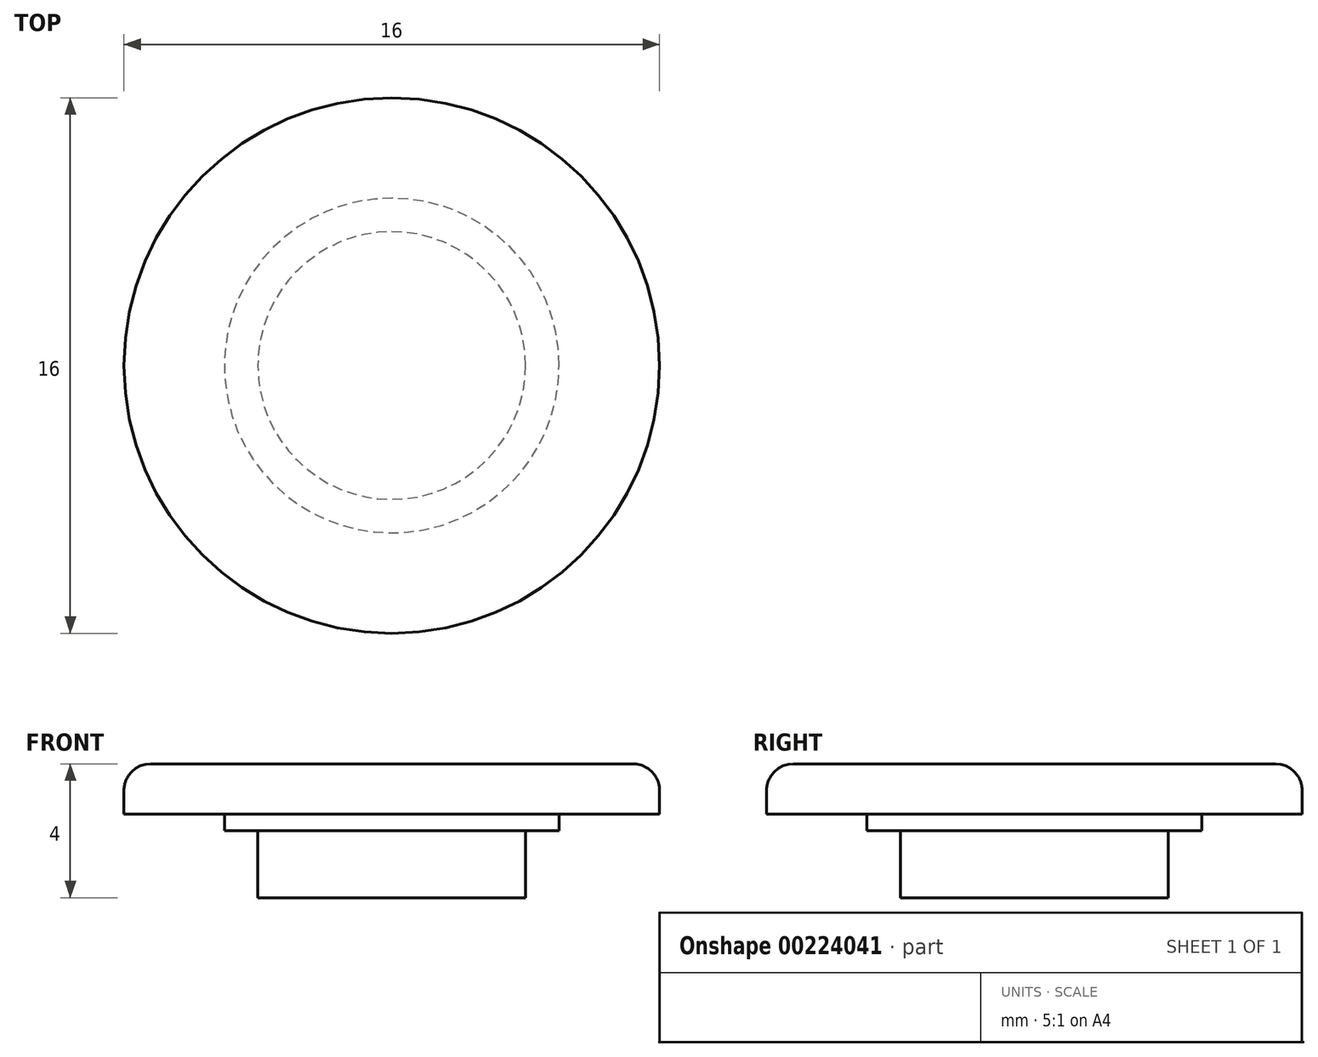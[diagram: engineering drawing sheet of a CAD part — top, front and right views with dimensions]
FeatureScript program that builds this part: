
annotation { "Feature Type Name" : "Feature", "Feature Type Description" : "" }
export const myFeature = defineFeature(function(context is Context, id is Id, definition is map)
    precondition{}
    {
        {
            var Q0;
            Q0=qCreatedBy(makeId("Front.planeOp"),FACE);
            var sketch = newSketch(context, id + "F0", { "sketchPlane" : qUnion([Q0])});
            skLineSegment(sketch, "E0", {"start": v(0, 0) * mm, "end": v(0, 4) * mm, "construction": true});
            skLineSegment(sketch, "E1", {"start": v(0, 4) * mm, "end": v(8, 4) * mm});
            skLineSegment(sketch, "E2", {"start": v(8, 4) * mm, "end": v(8, 2.5) * mm});
            skLineSegment(sketch, "E3", {"start": v(8, 2.5) * mm, "end": v(5, 2.5) * mm});
            skLineSegment(sketch, "E4", {"start": v(5, 2.5) * mm, "end": v(5, 2) * mm});
            skLineSegment(sketch, "E5", {"start": v(5, 2) * mm, "end": v(4, 2) * mm});
            skLineSegment(sketch, "E6", {"start": v(4, 2) * mm, "end": v(4, 0) * mm});
            skLineSegment(sketch, "E7", {"start": v(4, 0) * mm, "end": v(0, 0) * mm});
            skLineSegment(sketch, "E8", {"start": v(0, 4) * mm, "end": v(0, 0) * mm});
            skSolve(sketch);
        }
        {
            var Q0;
            Q0 = qSketchRegion(id + "F0", true);
            var Q1;
            Q1=sQuery(id+"F0.wireOp",EDGE,"E8");
            revolve(context, id + "F1", {"entities" : qUnion([Q0]), "axis" : qUnion([Q1]), "revolveType" : RevolveType.FULL});
        }
        {
            var Q0;
            Q0=makeQuery(id+"F1.opRevolve","SWEPT_EDGE",EDGE,{"disambiguationData":[OSD([sQuery(id+"F0.wireOp",EDGE,"E1"),sQuery(id+"F0.wireOp",EDGE,"E2")])]});
            fillet(context, id + "F2", {"entities" : qUnion([Q0]), "radius" : 0.8 * mm, "tangentPropagation" : true, "allowEdgeOverflow" : false});
        }
    });
